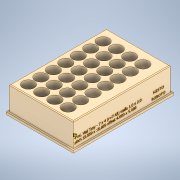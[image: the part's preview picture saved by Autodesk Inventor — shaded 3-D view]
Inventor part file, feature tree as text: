
AUTODESK INVENTOR PART (.ipt)
format: ipt  version: 2020 (Build 240168000, 168)  size: 2,261,504 bytes
history: native  units: in
note: dims shown in document units (in); Inventor stores cm internally (conversion verified against a paired STEP export)
features: sketch x4, extrude x2, hole x1, pattern_linear x1, fillet x1, emboss x1
ambient origin geometry x8: Origin, YZ Plane, XZ Plane, XY Plane, X Axis, Y Axis, Z Axis, Center Point
bodies: Solid1 (feature_tree)
feature tree (10):
  extrude  "Extrusion1"  TaperAngle=45.0deg  [1 undecoded]
  extrude  "Extrusion2"  TaperAngle=225.0deg  [1 undecoded]
  hole  "Hole2"  [1 undecoded]
  pattern_linear  "Rectangular Pattern1"  Spacing1=0.585in  [1 undecoded]
  fillet  "Fillet1"  Radius=0.75in
  emboss  "Emboss2"
  sketch  "Sketch1"  dims[d3=0.0in d5=45.0deg]
  sketch  "Sketch2"  dims[d6=0.1181in d7=225.0deg]
  sketch  "Sketch4"  dims[d9=0.0in d30=0.673in]
  sketch  "Sketch5"  dims[d31=45.0deg d32=0.585in d33=0.75in d34=0.375in d35=0.25in d36=0.5635in d38=0.0in d41=0.6244in d44=0.6637in d48=0.0394in d49=0.0in]
note: 4 required parameter values undecoded (feature->parameter linkage not recoverable at this tier; creation-order binding heuristic only, values carry confidence <= 0.55)
